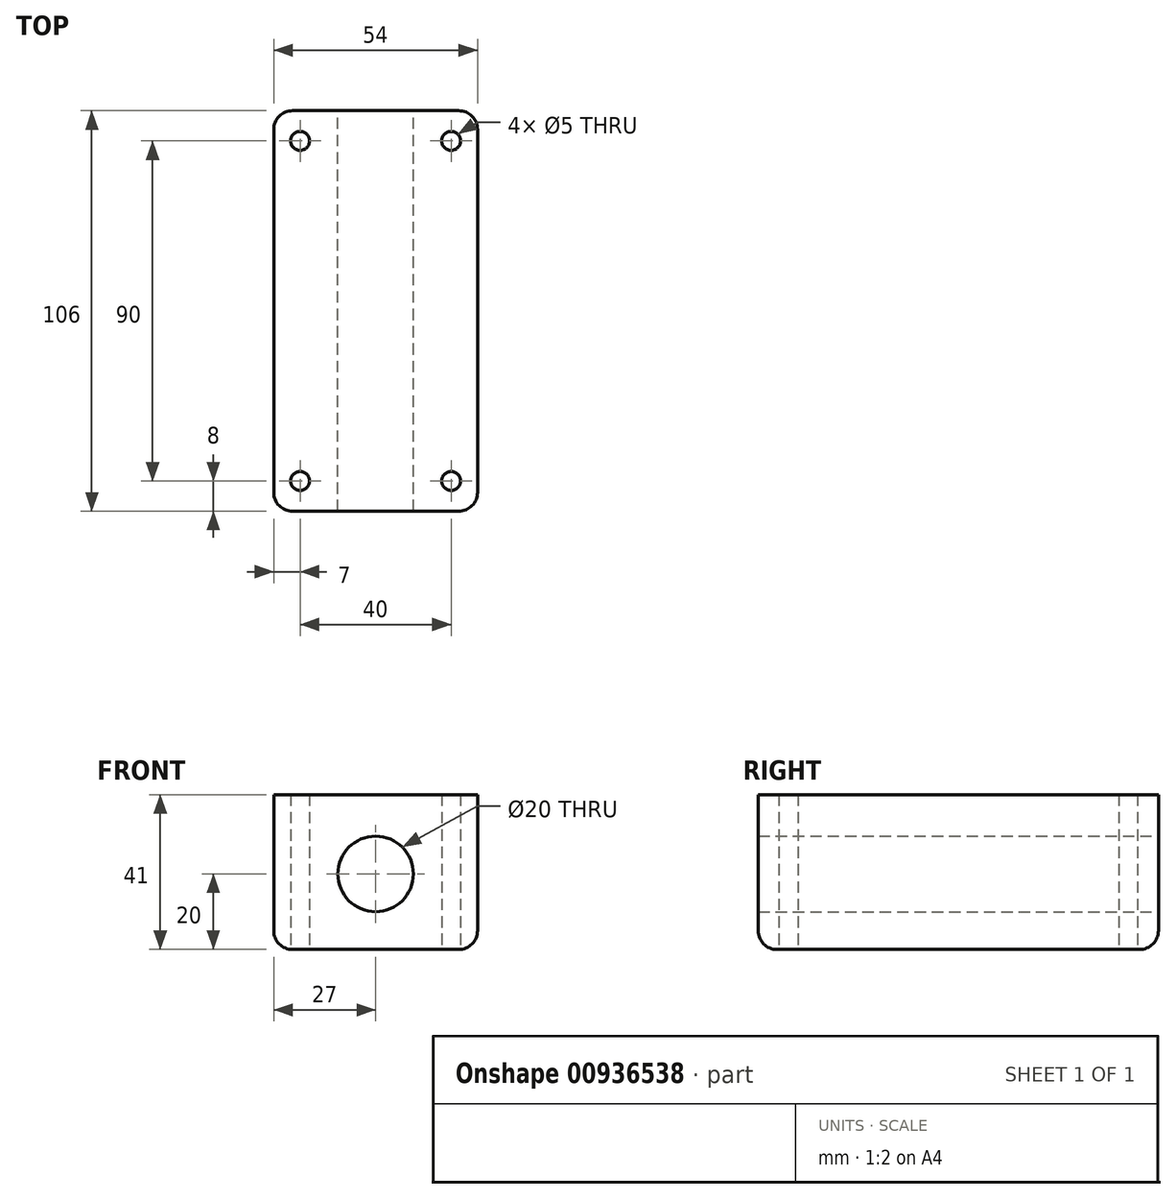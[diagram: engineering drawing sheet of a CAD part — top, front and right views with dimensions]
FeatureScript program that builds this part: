
annotation { "Feature Type Name" : "Feature", "Feature Type Description" : "" }
export const myFeature = defineFeature(function(context is Context, id is Id, definition is map)
    precondition{}
    {
        {
            var Q0;
            Q0=qCreatedBy(makeId("Front.planeOp"),FACE);
            var sketch = newSketch(context, id + "F0", { "sketchPlane" : qUnion([Q0])});
            skLineSegment(sketch, "E0.bottom", {"start": v(27, 20.5) * mm, "end": v(-27, 20.5) * mm});
            skLineSegment(sketch, "E0.top", {"start": v(27, -20.5) * mm, "end": v(-27, -20.5) * mm});
            skLineSegment(sketch, "E0.left", {"start": v(27, 20.5) * mm, "end": v(27, -20.5) * mm});
            skLineSegment(sketch, "E0.right", {"start": v(-27, 20.5) * mm, "end": v(-27, -20.5) * mm});
            skPoint(sketch, "E0.middle", {"position": v(0, 0) * mm});
            skCircle(sketch, "E1", {"center": v(0, -0.5) * mm, "radius": 10 * mm});
            skSolve(sketch);
        }
        {
            var Q0;
            Q0=makeQuery(id+"F0.imprint","IMPRINT",FACE,{"disambiguationData":[TD([[makeQuery(id+"F0.imprint","IMPRINT",EDGE,{"derivedFrom":sQuery(id+"F0.wireOp",EDGE,"E0.bottom")}),1.0]])]});
            extrude(context, id + "F1", {"entities" : qUnion([Q0]), "depth" : 106 * mm, "offsetDistance" : 25 * mm});
        }
        {
            var Q0;
            Q0=makeQuery(id+"F1.opExtrude","SWEPT_FACE",FACE,{"disambiguationData":[OSD([sQuery(id+"F0.wireOp",EDGE,"E0.bottom")])]});
            var sketch = newSketch(context, id + "F2", { "sketchPlane" : qUnion([Q0])});
            skLineSegment(sketch, "E2", {"start": v(0, 0) * mm, "end": v(0, -106) * mm, "construction": true});
            skPoint(sketch, "E3", {"position": v(-20, -8) * mm});
            skPoint(sketch, "E4", {"position": v(-20, -98) * mm});
            skPoint(sketch, "E5.MirrorP", {"position": v(20, -8) * mm});
            skPoint(sketch, "E6.MirrorP", {"position": v(20, -98) * mm});
            skSolve(sketch);
        }
        {
            var Q0;
            Q0=sQuery(id+"F2.wireOp",VERTEX,"E3");
            var Q1;
            Q1=sQuery(id+"F2.wireOp",VERTEX,"E5.MirrorP");
            var Q2;
            Q2=sQuery(id+"F2.wireOp",VERTEX,"E4");
            var Q3;
            Q3=sQuery(id+"F2.wireOp",VERTEX,"E6.MirrorP");
            var Q4;
            Q4=makeQuery(id+"F1.opExtrude","SWEPT_BODY",BODY,{"disambiguationData":[OSD([sQuery(id+"F0.wireOp",EDGE,"E0.bottom"),sQuery(id+"F0.wireOp",EDGE,"E0.top"),sQuery(id+"F0.wireOp",EDGE,"E0.left"),sQuery(id+"F0.wireOp",EDGE,"E0.right"),sQuery(id+"F0.wireOp",EDGE,"E1")])]});
            hole(context, id + "F3", {"style" : HoleStyle.SIMPLE, "endStyle" : HoleEndStyle.THROUGH, "standardTappedOrClearance" : lookupTablePath({ "standard" : "ISO", "engagement" : "75%", "pitch" : "1 mm", "size" : "M6", "type" : "Tapped" }), "standardBlindInLast" : lookupTablePath({ "standard" : "ISO", "engagement" : "75%", "pitch" : "1 mm", "size" : "M6", "type" : "Tapped" }), "holeDiameter" : 5 * mm, "majorDiameter" : 6 * mm, "showTappedDepth" : true, "tappedDepth" : 12 * mm, "tapClearance" : 3, "locations" : qUnion([Q0, Q1, Q2, Q3]), "scope" : qUnion([Q4]), "startStyle" : HoleStartStyle.PART});
        }
        {
            var Q0;
            Q0=makeQuery(id+"F1.opExtrude","CAP_EDGE",EDGE,{"disambiguationData":[OSD([sQuery(id+"F0.wireOp",EDGE,"E0.right")])],"isStart":false});
            var Q1;
            Q1=makeQuery(id+"F1.opExtrude","CAP_EDGE",EDGE,{"disambiguationData":[OSD([sQuery(id+"F0.wireOp",EDGE,"E0.top")])],"isStart":false});
            var Q2;
            Q2=makeQuery(id+"F1.opExtrude","CAP_EDGE",EDGE,{"disambiguationData":[OSD([sQuery(id+"F0.wireOp",EDGE,"E0.left")])],"isStart":false});
            var Q3;
            Q3=makeQuery(id+"F1.opExtrude","CAP_EDGE",EDGE,{"disambiguationData":[OSD([sQuery(id+"F0.wireOp",EDGE,"E0.left")])],"isStart":true});
            var Q4;
            Q4=makeQuery(id+"F1.opExtrude","CAP_EDGE",EDGE,{"disambiguationData":[OSD([sQuery(id+"F0.wireOp",EDGE,"E0.top")])],"isStart":true});
            var Q5;
            Q5=makeQuery(id+"F1.opExtrude","CAP_EDGE",EDGE,{"disambiguationData":[OSD([sQuery(id+"F0.wireOp",EDGE,"E0.right")])],"isStart":true});
            var Q6;
            Q6=makeQuery(id+"F1.opExtrude","SWEPT_EDGE",EDGE,{"disambiguationData":[OSD([sQuery(id+"F0.wireOp",EDGE,"E0.top"),sQuery(id+"F0.wireOp",EDGE,"E0.left")])]});
            var Q7;
            Q7=makeQuery(id+"F1.opExtrude","SWEPT_EDGE",EDGE,{"disambiguationData":[OSD([sQuery(id+"F0.wireOp",EDGE,"E0.top"),sQuery(id+"F0.wireOp",EDGE,"E0.right")])]});
            fillet(context, id + "F4", {"entities" : qUnion([Q0, Q1, Q2, Q3, Q4, Q5, Q6, Q7]), "radius" : 5 * mm, "tangentPropagation" : true, "allowEdgeOverflow" : false});
        }
    });
